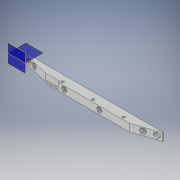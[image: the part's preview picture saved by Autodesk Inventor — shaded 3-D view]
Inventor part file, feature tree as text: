
AUTODESK INVENTOR PART (.ipt)
format: ipt  version: 2019 (Build 230136000, 136)  size: 178,688 bytes
history: native  units: in
note: dims shown in document units (in); Inventor stores cm internally (conversion verified against a paired STEP export)
features: plane x7, other x3
ambient origin geometry x8: Origin, YZ Plane, XZ Plane, XY Plane, X Axis, Y Axis, Z Axis, Center Point
bodies: Solid1 (feature_tree)
feature tree (10):
  other  "wheel_support_v5_narrow_with_line_sensor_all_holes.ipt"
  other  "Solid1::wheel_support_v5_narrow_with_line_sensor_all_holes.ipt"
  other  "TaggingFeature1"
  plane  "Work Plane1"
  plane  "Work Plane2"
  plane  "Work Plane3"
  plane  "Work Plane4"
  plane  "Work Plane5"
  plane  "Work Plane6"
  plane  "Work Plane7"
